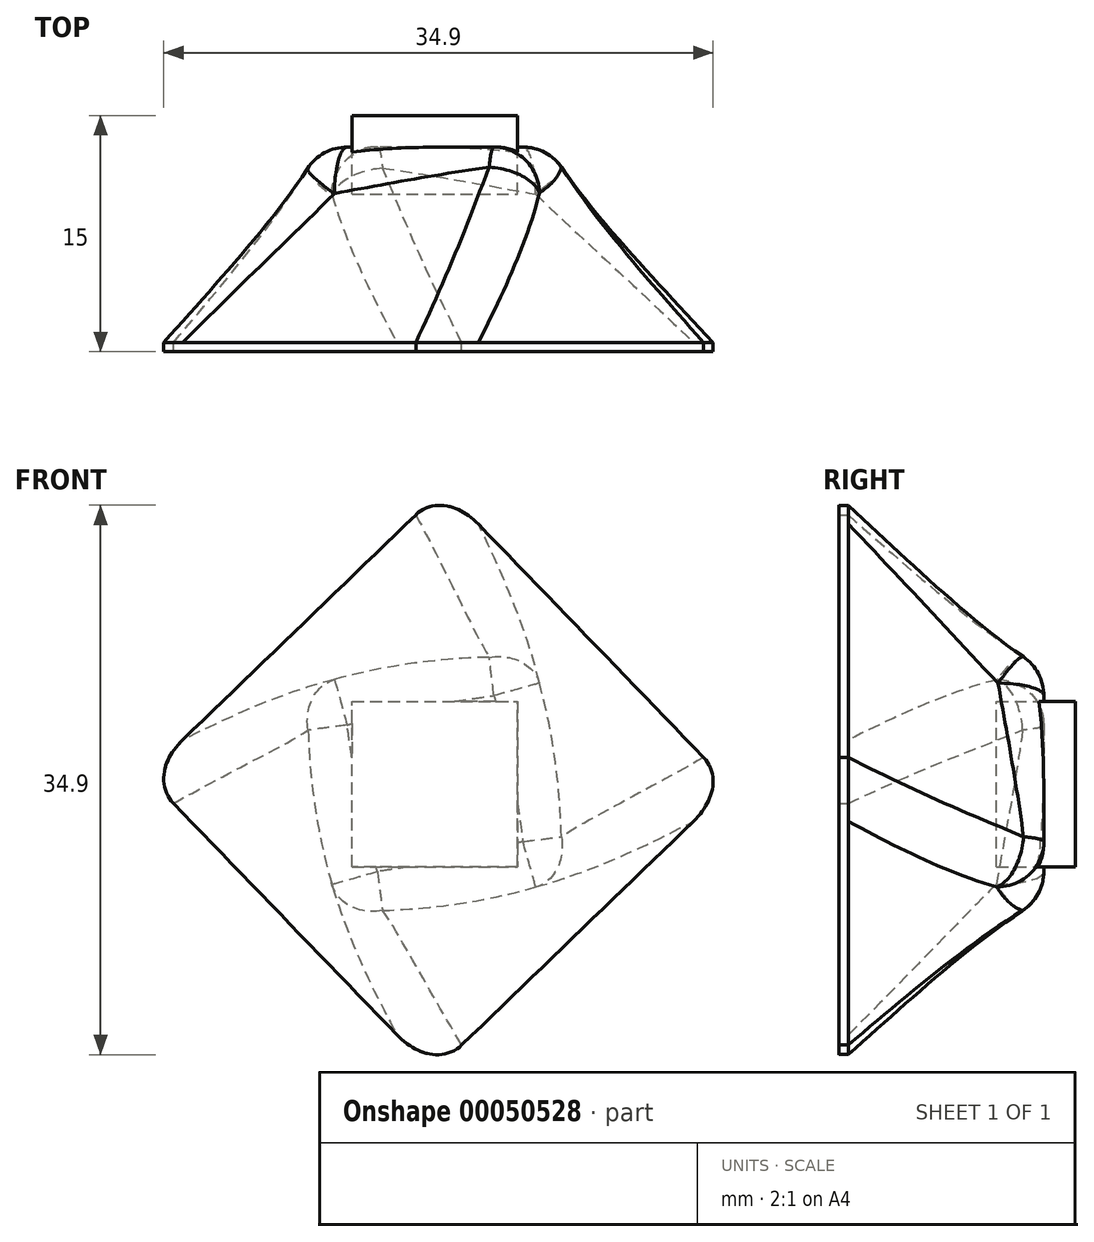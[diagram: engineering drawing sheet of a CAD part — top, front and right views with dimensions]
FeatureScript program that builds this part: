
annotation { "Feature Type Name" : "Feature", "Feature Type Description" : "" }
export const myFeature = defineFeature(function(context is Context, id is Id, definition is map)
    precondition{}
    {
        {
            var Q0;
            Q0=qCreatedBy(makeId("Front.planeOp"),FACE);
            var sketch = newSketch(context, id + "F0", { "sketchPlane" : qUnion([Q0])});
            skLineSegment(sketch, "E0.bottom", {"start": v(-5.5, -5.5) * mm, "end": v(5, -5.5) * mm});
            skLineSegment(sketch, "E0.top", {"start": v(-5.5, 5) * mm, "end": v(5, 5) * mm});
            skLineSegment(sketch, "E0.left", {"start": v(-5.5, -5.5) * mm, "end": v(-5.5, 5) * mm});
            skLineSegment(sketch, "E0.right", {"start": v(5, -5.5) * mm, "end": v(5, 5) * mm});
            skLineSegment(sketch, "E1.0", {"start": v(-7.5, 7) * mm, "end": v(7, 7) * mm});
            skLineSegment(sketch, "E1.1", {"start": v(-7.5, -7.5) * mm, "end": v(-7.5, 7) * mm});
            skLineSegment(sketch, "E1.2", {"start": v(-7.5, -7.5) * mm, "end": v(7, -7.5) * mm});
            skLineSegment(sketch, "E1.3", {"start": v(7, -7.5) * mm, "end": v(7, 7) * mm});
            skCircle(sketch, "E2.cCircle", {"center": v(0, 0) * mm, "radius": 19.1 * mm, "construction": true});
            skLineSegment(sketch, "E2.0", {"start": v(0, 19.1) * mm, "end": v(19.1, 0) * mm});
            skLineSegment(sketch, "E2.1", {"start": v(19.1, 0) * mm, "end": v(0, -19.1) * mm});
            skLineSegment(sketch, "E2.2", {"start": v(0, -19.1) * mm, "end": v(-19.1, 0) * mm});
            skLineSegment(sketch, "E2.3", {"start": v(-19.1, 0) * mm, "end": v(0, 19.1) * mm});
            skSolve(sketch);
        }
        {
            var Q0;
            Q0=makeQuery(id+"F0.imprint","IMPRINT",FACE,{"disambiguationData":[TD([[makeQuery(id+"F0.imprint","IMPRINT",EDGE,{"derivedFrom":sQuery(id+"F0.wireOp",EDGE,"E0.bottom")}),1.0]])]});
            extrude(context, id + "F1", {"entities" : qUnion([Q0]), "depth" : 5 * mm});
        }
        {
            var Q0;
            Q0=qCreatedBy(makeId("Front.planeOp"),FACE);
            cPlane(context, id + "F2", {"entities" : qUnion([Q0]), "cplaneType" : CPlaneType.OFFSET, "offset" : 2 * mm, "width" : 150 * mm, "height" : 150 * mm});
        }
        {
            var Q0;
            Q0=qCreatedBy(id+"F2.planeOp",FACE);
            cPlane(context, id + "F3", {"entities" : qUnion([Q0]), "cplaneType" : CPlaneType.OFFSET, "offset" : 13 * mm, "width" : 150 * mm, "height" : 150 * mm});
        }
        {
            var Q0;
            Q0=qCreatedBy(id+"F3.planeOp",FACE);
            var sketch = newSketch(context, id + "F4", { "sketchPlane" : qUnion([Q0])});
            skLineSegment(sketch, "E3.0", {"start": v(-19.1, 0) * mm, "end": v(0, 19.1) * mm});
            skLineSegment(sketch, "E4.0.0", {"start": v(19.1, 0) * mm, "end": v(0, 19.1) * mm});
            skLineSegment(sketch, "E4.0.1", {"start": v(0, 19.1) * mm, "end": v(-19.1, 0) * mm});
            skLineSegment(sketch, "E4.0.2", {"start": v(-19.1, 0) * mm, "end": v(0, -19.1) * mm});
            skLineSegment(sketch, "E4.0.3", {"start": v(0, -19.1) * mm, "end": v(19.1, 0) * mm});
            skSolve(sketch);
        }
        {
            var Q0;
            Q0=qCreatedBy(id+"F2.planeOp",FACE);
            var sketch = newSketch(context, id + "F5", { "sketchPlane" : qUnion([Q0])});
            skLineSegment(sketch, "E5.0.0", {"start": v(7, 7) * mm, "end": v(-7.5, 7) * mm});
            skLineSegment(sketch, "E5.0.1", {"start": v(-7.5, 7) * mm, "end": v(-7.5, -7.5) * mm});
            skLineSegment(sketch, "E5.0.2", {"start": v(-7.5, -7.5) * mm, "end": v(7, -7.5) * mm});
            skLineSegment(sketch, "E5.0.3", {"start": v(7, -7.5) * mm, "end": v(7, 7) * mm});
            skSolve(sketch);
        }
        {
            var Q0;
            Q0=sQuery(id+"F4.wireOp",VERTEX,"E4.0.2.start");
            var Q1;
            Q1=sQuery(id+"F5.wireOp",VERTEX,"E5.0.1.start");
            var Q2;
            Q2=sQuery(id+"F0.wireOp",VERTEX,"E1.1.end");
            cPlane(context, id + "F6", {"entities" : qUnion([Q0, Q1, Q2]), "cplaneType" : CPlaneType.THREE_POINT, "offset" : 150 * mm, "width" : 150 * mm, "height" : 150 * mm});
        }
        {
            var Q0;
            Q0=qCreatedBy(id+"F6.planeOp",FACE);
            var sketch = newSketch(context, id + "F7", { "sketchPlane" : qUnion([Q0])});
            skPoint(sketch, "E6.0", {"position": v(-16.34, 15) * mm});
            skPoint(sketch, "E7.0", {"position": v(-2.8, 2) * mm});
            skLineSegment(sketch, "E8", {"start": v(-16.34, 15) * mm, "end": v(-2.8, 2) * mm});
            skSolve(sketch);
        }
        {
            var Q0;
            Q0=makeQuery(id+"F5.imprint","IMPRINT",FACE,{"disambiguationData":[TD([[makeQuery(id+"F5.imprint","IMPRINT",EDGE,{"derivedFrom":sQuery(id+"F5.wireOp",EDGE,"E5.0.0")}),1.0]])]});
            var Q1;
            Q1=makeQuery(id+"F4.imprint","IMPRINT",FACE,{"disambiguationData":[TD([[makeQuery(id+"F4.imprint","IMPRINT",EDGE,{"derivedFrom":sQuery(id+"F4.wireOp",EDGE,"E4.0.0")}),1.0]])]});
            var Q2;
            Q2=sQuery(id+"F7.wireOp",EDGE,"E8");
            loft(context, id + "F8", {"sheetProfilesArray" : [{ "sheetProfileEntities" : qUnion([Q0]) }, { "sheetProfileEntities" : qUnion([Q1]) }], "guidesArray" : [{ "guideEntities" : qUnion([Q2]), "guideDerivativeType" : LoftGuideDerivativeType.DEFAULT, "guideDerivativeMagnitude" : 1 }]});
        }
        {
            var Q0;
            Q0=makeQuery(id+"F1.opExtrude","SWEPT_BODY",BODY,{"disambiguationData":[OSD([sQuery(id+"F0.wireOp",EDGE,"E0.bottom"),sQuery(id+"F0.wireOp",EDGE,"E0.top"),sQuery(id+"F0.wireOp",EDGE,"E0.left"),sQuery(id+"F0.wireOp",EDGE,"E0.right")])]});
            var Q1;
            Q1=makeQuery(id+"F8.opLoft","SWEPT_BODY",BODY,{"disambiguationData":[OSD([makeQuery(id+"F4.imprint","IMPRINT",FACE,{"disambiguationData":[TD([[makeQuery(id+"F4.imprint","IMPRINT",EDGE,{"derivedFrom":sQuery(id+"F4.wireOp",EDGE,"E4.0.0")}),1.0]])]}),makeQuery(id+"F5.imprint","IMPRINT",FACE,{"disambiguationData":[TD([[makeQuery(id+"F5.imprint","IMPRINT",EDGE,{"derivedFrom":sQuery(id+"F5.wireOp",EDGE,"E5.0.0")}),1.0]])]})])]});
            booleanBodies(context, id + "F9", {"operationType" : BooleanOperationType.SUBTRACTION, "tools" : qUnion([Q0]), "targets" : qUnion([Q1]), "keepTools" : true});
        }
        {
            var Q0;
            Q0=makeQuery(id+"F8.opLoft","SWEPT_EDGE",EDGE,{"disambiguationData":[OSD([sQuery(id+"F4.wireOp",EDGE,"E4.0.0"),sQuery(id+"F4.wireOp",EDGE,"E4.0.3"),sQuery(id+"F5.wireOp",EDGE,"E5.0.0"),sQuery(id+"F5.wireOp",EDGE,"E5.0.3")])]});
            var Q1;
            Q1=makeQuery(id+"F8.opLoft","SWEPT_EDGE",EDGE,{"disambiguationData":[OSD([sQuery(id+"F4.wireOp",EDGE,"E4.0.0"),sQuery(id+"F4.wireOp",EDGE,"E4.0.1"),sQuery(id+"F5.wireOp",EDGE,"E5.0.0"),sQuery(id+"F5.wireOp",EDGE,"E5.0.1")])]});
            var Q2;
            Q2=makeQuery(id+"F8.opLoft","SWEPT_EDGE",EDGE,{"disambiguationData":[OSD([sQuery(id+"F4.wireOp",EDGE,"E4.0.1"),sQuery(id+"F4.wireOp",EDGE,"E4.0.2"),sQuery(id+"F5.wireOp",EDGE,"E5.0.1"),sQuery(id+"F5.wireOp",EDGE,"E5.0.2")])]});
            var Q3;
            Q3=makeQuery(id+"F8.opLoft","SWEPT_EDGE",EDGE,{"disambiguationData":[OSD([sQuery(id+"F4.wireOp",EDGE,"E4.0.2"),sQuery(id+"F4.wireOp",EDGE,"E4.0.3"),sQuery(id+"F5.wireOp",EDGE,"E5.0.2"),sQuery(id+"F5.wireOp",EDGE,"E5.0.3")])]});
            var Q4;
            Q4=makeQuery(id+"F8.opLoft","MID_CAP_EDGE",EDGE,{"disambiguationData":[OSD([sQuery(id+"F5.wireOp",EDGE,"E5.0.0"),sQuery(id+"F5.wireOp",EDGE,"E5.0.1"),sQuery(id+"F5.wireOp",EDGE,"E5.0.2")])],"capPos":0.0});
            var Q5;
            Q5=makeQuery(id+"F8.opLoft","MID_CAP_EDGE",EDGE,{"disambiguationData":[OSD([sQuery(id+"F5.wireOp",EDGE,"E5.0.1"),sQuery(id+"F5.wireOp",EDGE,"E5.0.2"),sQuery(id+"F5.wireOp",EDGE,"E5.0.3")])],"capPos":0.0});
            var Q6;
            Q6=makeQuery(id+"F8.opLoft","MID_CAP_EDGE",EDGE,{"disambiguationData":[OSD([sQuery(id+"F5.wireOp",EDGE,"E5.0.0"),sQuery(id+"F5.wireOp",EDGE,"E5.0.2"),sQuery(id+"F5.wireOp",EDGE,"E5.0.3")])],"capPos":0.0});
            var Q7;
            Q7=makeQuery(id+"F8.opLoft","MID_CAP_EDGE",EDGE,{"disambiguationData":[OSD([sQuery(id+"F5.wireOp",EDGE,"E5.0.0"),sQuery(id+"F5.wireOp",EDGE,"E5.0.1"),sQuery(id+"F5.wireOp",EDGE,"E5.0.3")])],"capPos":0.0});
            fillet(context, id + "F10", {"entities" : qUnion([Q0, Q1, Q2, Q3, Q4, Q5, Q6, Q7]), "radius" : 3 * mm, "tangentPropagation" : true, "allowEdgeOverflow" : false});
        }
        {
            var Q0;
            Q0=makeQuery(id+"F8.opLoft","CAP_FACE",FACE,{"disambiguationData":[OSD([makeQuery(id+"F4.imprint","IMPRINT",FACE,{"disambiguationData":[TD([[makeQuery(id+"F4.imprint","IMPRINT",EDGE,{"derivedFrom":sQuery(id+"F4.wireOp",EDGE,"E4.0.0")}),1.0]])]})])],"isStart":true});
            chamfer(context, id + "F11", {"entities" : qUnion([Q0]), "chamferType" : ChamferType.OFFSET_ANGLE, "width" : .2 * mm, "oppositeDirection" : false, "angle" : 90 * degree, "tangentPropagation" : true});
        }
    });
